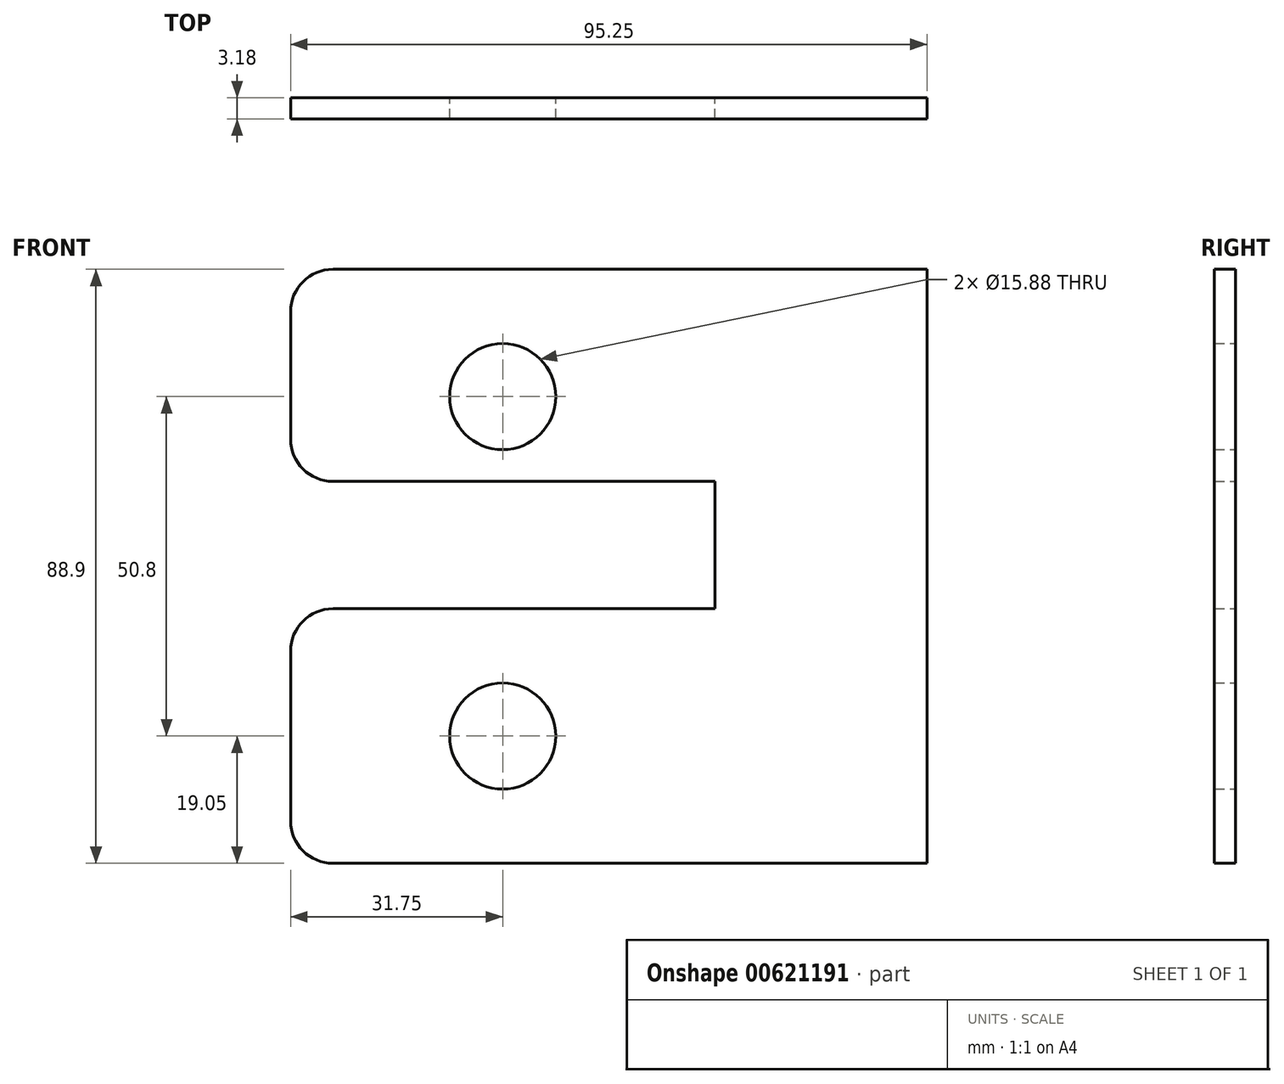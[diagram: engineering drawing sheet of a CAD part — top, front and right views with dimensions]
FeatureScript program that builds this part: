
annotation { "Feature Type Name" : "Feature", "Feature Type Description" : "" }
export const myFeature = defineFeature(function(context is Context, id is Id, definition is map)
    precondition{}
    {
        {
            var Q0;
            Q0=qCreatedBy(makeId("Front.planeOp"),FACE);
            var sketch = newSketch(context, id + "F0", { "sketchPlane" : qUnion([Q0])});
            skLineSegment(sketch, "E0.right", {"start": v(-107.95, 63.5) * mm, "end": v(-107.95, 82.55) * mm});
            skPoint(sketch, "E1.visualSharp", {"position": v(-107.95, 88.9) * mm});
            skArc(sketch, "E1.filletArc", {"start": v(-101.6, 88.9) * mm, "mid": v(-106.1, 87.04) * mm, "end": v(-107.95, 82.55) * mm});
            skCircle(sketch, "E2", {"center": v(-76.2, 69.85) * mm, "radius": 7.94 * mm});
            skCircle(sketch, "E3", {"center": v(-76.2, 19.05) * mm, "radius": 7.94 * mm});
            skArc(sketch, "E4.filletArc", {"start": v(-101.6, 38.1) * mm, "mid": v(-106.1, 36.24) * mm, "end": v(-107.95, 31.75) * mm});
            skLineSegment(sketch, "E5", {"start": v(-107.95, 88.9) * mm, "end": v(-12.7, 88.9) * mm});
            skLineSegment(sketch, "E6", {"start": v(-12.7, 88.9) * mm, "end": v(-12.7, 0) * mm});
            skLineSegment(sketch, "E7", {"start": v(-12.7, 0) * mm, "end": v(-95.25, 0) * mm});
            skLineSegment(sketch, "E8", {"start": v(-44.45, 57.15) * mm, "end": v(-44.45, 38.1) * mm});
            skLineSegment(sketch, "E9", {"start": v(-44.45, 38.1) * mm, "end": v(-101.6, 38.1) * mm});
            skLineSegment(sketch, "E10", {"start": v(-44.45, 57.15) * mm, "end": v(-101.6, 57.15) * mm});
            skPoint(sketch, "E11.visualSharp", {"position": v(-107.95, 57.15) * mm});
            skArc(sketch, "E11.filletArc", {"start": v(-107.95, 63.5) * mm, "mid": v(-106.1, 59) * mm, "end": v(-101.6, 57.15) * mm});
            skLineSegment(sketch, "E12", {"start": v(-95.25, 0) * mm, "end": v(-101.6, 0) * mm});
            skLineSegment(sketch, "E13", {"start": v(-107.95, 6.35) * mm, "end": v(-107.95, 31.75) * mm});
            skPoint(sketch, "E14.visualSharp", {"position": v(-107.95, 0) * mm});
            skArc(sketch, "E14.filletArc", {"start": v(-107.95, 6.35) * mm, "mid": v(-106.1, 1.86) * mm, "end": v(-101.6, 0) * mm});
            skLineSegment(sketch, "E15", {"start": v(-44.45, 0) * mm, "end": v(-44.45, 38.1) * mm});
            skLineSegment(sketch, "E16", {"start": v(-44.45, 57.15) * mm, "end": v(-44.45, 88.9) * mm});
            skSolve(sketch);
        }
        {
            var Q0;
            Q0=makeQuery(id+"F0.imprint","IMPRINT",FACE,{"disambiguationData":[TD([[makeQuery(id+"F0.imprint","IMPRINT",EDGE,{"derivedFrom":sQuery(id+"F0.wireOp",EDGE,"E0.bottom")}),-1.0]])]});
            var Q1;
            Q1=makeQuery(id+"F0.imprint","IMPRINT",FACE,{"disambiguationData":[TD([[makeQuery(id+"F0.imprint","IMPRINT",EDGE,{"derivedFrom":sQuery(id+"F0.wireOp",EDGE,"E0.right")}),-1.0]])]});
            var Q2;
            {var subQ1=sQuery(id+"F0.wireOp",EDGE,"E6");Q2=makeQuery(id+"F0.imprint","IMPRINT",FACE,{"disambiguationData":[TD([[makeQuery(id+"F0.imprint","IMPRINT",EDGE,{"derivedFrom":subQ1}),-1.0]])]});}
            var Q3;
            Q3=makeQuery(id+"F0.imprint","IMPRINT",FACE,{"disambiguationData":[TD([[makeQuery(id+"F0.imprint","IMPRINT",EDGE,{"derivedFrom":sQuery(id+"F0.wireOp",EDGE,"E3")}),-1.0]])]});
            extrude(context, id + "F1", {"entities" : qUnion([Q0, Q1, Q2, Q3]), "depth" : 3.17 * mm, "offsetDistance" : 25.4 * mm});
        }
    });
